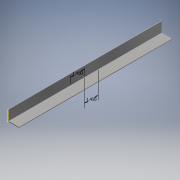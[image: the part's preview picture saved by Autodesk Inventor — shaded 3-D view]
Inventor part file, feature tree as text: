
AUTODESK INVENTOR PART (.ipt)
format: ipt  version: 2017 (Build 210142000, 142)  size: 123,904 bytes
history: native  units: in
note: dims shown in document units (in); Inventor stores cm internally (conversion verified against a paired STEP export)
features: sketch x5, extrude x3
ambient origin geometry x8: Origin, YZ Plane, XZ Plane, XY Plane, X Axis, Y Axis, Z Axis, Center Point
bodies: Solid1 (feature_tree)
feature tree (8):
  extrude  "Extrusion1"  Depth=1.1in
  extrude  "Extrusion2"  Depth=0.06in
  sketch  "Sketch3"  dims[d5=1.1in d6=0.0in d7=1.45in]
  sketch  "Sketch4"  dims[d8=1.45in]
  extrude  "Extrusion4"  Depth=1.1in
  sketch  "Sketch1"  dims[d0=16.0in d1=1.1in]
  sketch  "Sketch2"  dims[d2=0.06in d3=0.0in d4=0.06in]
  sketch  "Sketch6"  dims[d11=0.6875in d12=0.0in]
